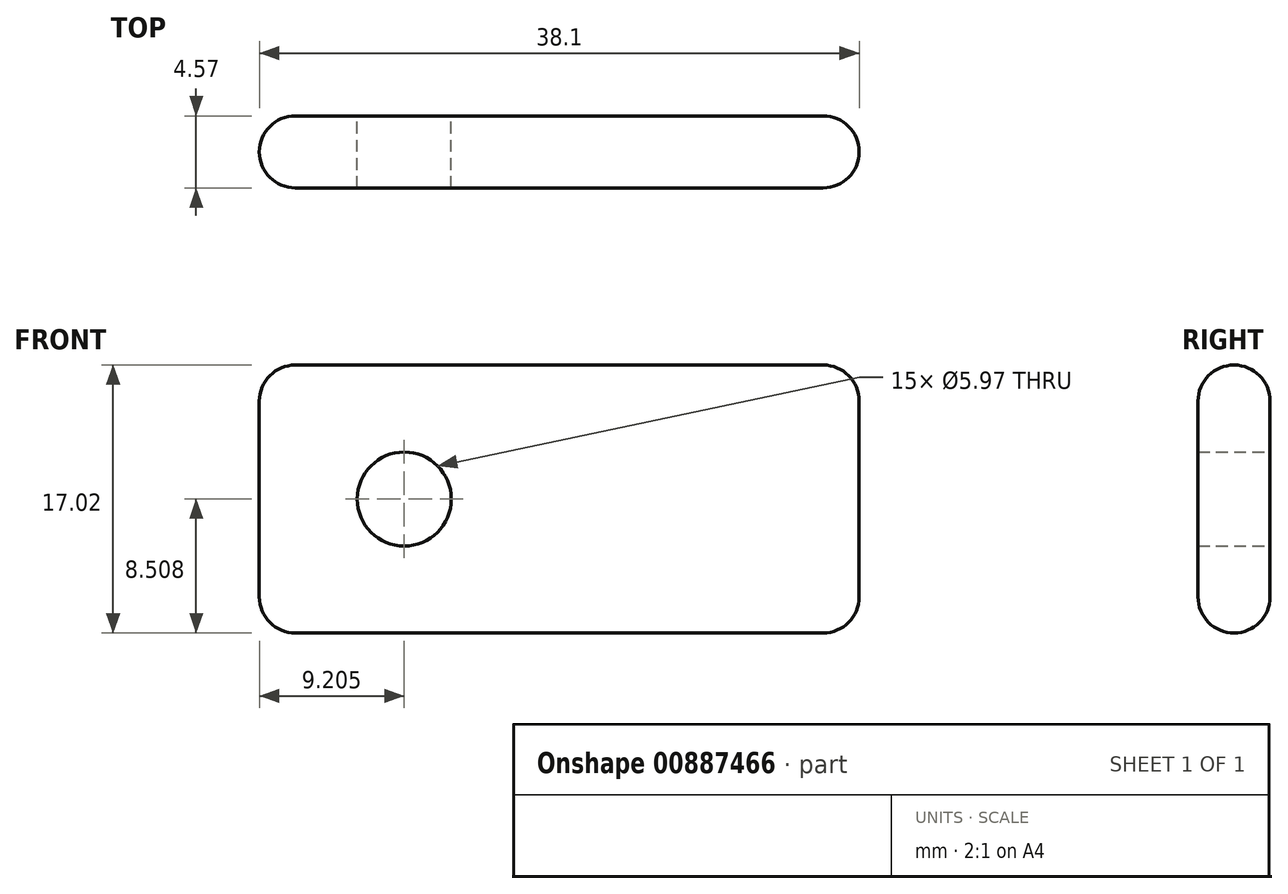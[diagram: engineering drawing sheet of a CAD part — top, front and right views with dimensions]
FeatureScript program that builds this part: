
annotation { "Feature Type Name" : "Feature", "Feature Type Description" : "" }
export const myFeature = defineFeature(function(context is Context, id is Id, definition is map)
    precondition{}
    {
        {
            var Q0;
            Q0=qCreatedBy(makeId("Front.planeOp"),FACE);
            var sketch = newSketch(context, id + "F0", { "sketchPlane" : qUnion([Q0])});
            skLineSegment(sketch, "E0.bottom", {"start": v(-67.2, -17.66) * mm, "end": v(-29.1, -17.66) * mm});
            skLineSegment(sketch, "E0.top", {"start": v(-67.2, -34.68) * mm, "end": v(-29.1, -34.68) * mm});
            skLineSegment(sketch, "E0.left", {"start": v(-67.2, -17.66) * mm, "end": v(-67.2, -34.68) * mm});
            skLineSegment(sketch, "E0.right", {"start": v(-29.1, -17.66) * mm, "end": v(-29.1, -34.68) * mm});
            skCircle(sketch, "E1", {"center": v(-58, -26.17) * mm, "radius": 2.98 * mm});
            skLineSegment(sketch, "E2", {"start": v(-67.2, -26.17) * mm, "end": v(-29.1, -26.17) * mm});
            skPoint(sketch, "E2.endSnap0", {"position": v(-29.1, -26.17) * mm});
            skSolve(sketch);
        }
        {
            var Q0;
            {var subQ5=sQuery(id+"F0.wireOp",EDGE,"E0.bottom");Q0=makeQuery(id+"F0.imprint","IMPRINT",FACE,{"disambiguationData":[TD([[makeQuery(id+"F0.imprint","IMPRINT",EDGE,{"derivedFrom":subQ5}),-1.0]])]});}
            var Q1;
            {var subQ5=sQuery(id+"F0.wireOp",EDGE,"E0.top");Q1=makeQuery(id+"F0.imprint","IMPRINT",FACE,{"disambiguationData":[TD([[makeQuery(id+"F0.imprint","IMPRINT",EDGE,{"derivedFrom":subQ5}),1.0]])]});}
            extrude(context, id + "F1", {"entities" : qUnion([Q0, Q1]), "depth" : 4.57 * mm, "offsetDistance" : 25.4 * mm});
        }
        {
            var Q0;
            Q0=makeQuery(id+"F1.opExtrude","SWEPT_EDGE",EDGE,{"disambiguationData":[OSD([sQuery(id+"F0.wireOp",EDGE,"E0.bottom"),sQuery(id+"F0.wireOp",EDGE,"E0.left")])]});
            var Q1;
            Q1=makeQuery(id+"F1.opExtrude","SWEPT_EDGE",EDGE,{"disambiguationData":[OSD([sQuery(id+"F0.wireOp",EDGE,"E0.bottom"),sQuery(id+"F0.wireOp",EDGE,"E0.right")])]});
            var Q2;
            Q2=makeQuery(id+"F1.opExtrude","SWEPT_EDGE",EDGE,{"disambiguationData":[OSD([sQuery(id+"F0.wireOp",EDGE,"E0.top"),sQuery(id+"F0.wireOp",EDGE,"E0.right")])]});
            var Q3;
            Q3=makeQuery(id+"F1.opExtrude","SWEPT_EDGE",EDGE,{"disambiguationData":[OSD([sQuery(id+"F0.wireOp",EDGE,"E0.top"),sQuery(id+"F0.wireOp",EDGE,"E0.left")])]});
            var Q4;
            Q4=makeQuery(id+"F1.opExtrude","CAP_EDGE",EDGE,{"disambiguationData":[OSD([sQuery(id+"F0.wireOp",EDGE,"E0.top")])],"isStart":false});
            var Q5;
            Q5=makeQuery(id+"F1.opExtrude","CAP_EDGE",EDGE,{"disambiguationData":[OSD([sQuery(id+"F0.wireOp",EDGE,"E0.top")])],"isStart":true});
            var Q6;
            Q6=makeQuery(id+"F1.opExtrude","CAP_EDGE",EDGE,{"disambiguationData":[OSD([sQuery(id+"F0.wireOp",EDGE,"E0.right")])],"isStart":true});
            var Q7;
            Q7=makeQuery(id+"F1.opExtrude","CAP_EDGE",EDGE,{"disambiguationData":[OSD([sQuery(id+"F0.wireOp",EDGE,"E0.right")])],"isStart":false});
            var Q8;
            Q8=makeQuery(id+"F1.opExtrude","CAP_EDGE",EDGE,{"disambiguationData":[OSD([sQuery(id+"F0.wireOp",EDGE,"E0.bottom")])],"isStart":false});
            var Q9;
            Q9=makeQuery(id+"F1.opExtrude","CAP_EDGE",EDGE,{"disambiguationData":[OSD([sQuery(id+"F0.wireOp",EDGE,"E0.bottom")])],"isStart":true});
            var Q10;
            Q10=makeQuery(id+"F1.opExtrude","CAP_EDGE",EDGE,{"disambiguationData":[OSD([sQuery(id+"F0.wireOp",EDGE,"E0.left")])],"isStart":true});
            var Q11;
            Q11=makeQuery(id+"F1.opExtrude","CAP_EDGE",EDGE,{"disambiguationData":[OSD([sQuery(id+"F0.wireOp",EDGE,"E0.left")])],"isStart":false});
            fillet(context, id + "F2", {"entities" : qUnion([Q0, Q1, Q2, Q3, Q4, Q5, Q6, Q7, Q8, Q9, Q10, Q11]), "radius" : 2.3 * mm, "tangentPropagation" : true, "allowEdgeOverflow" : false});
        }
    });
